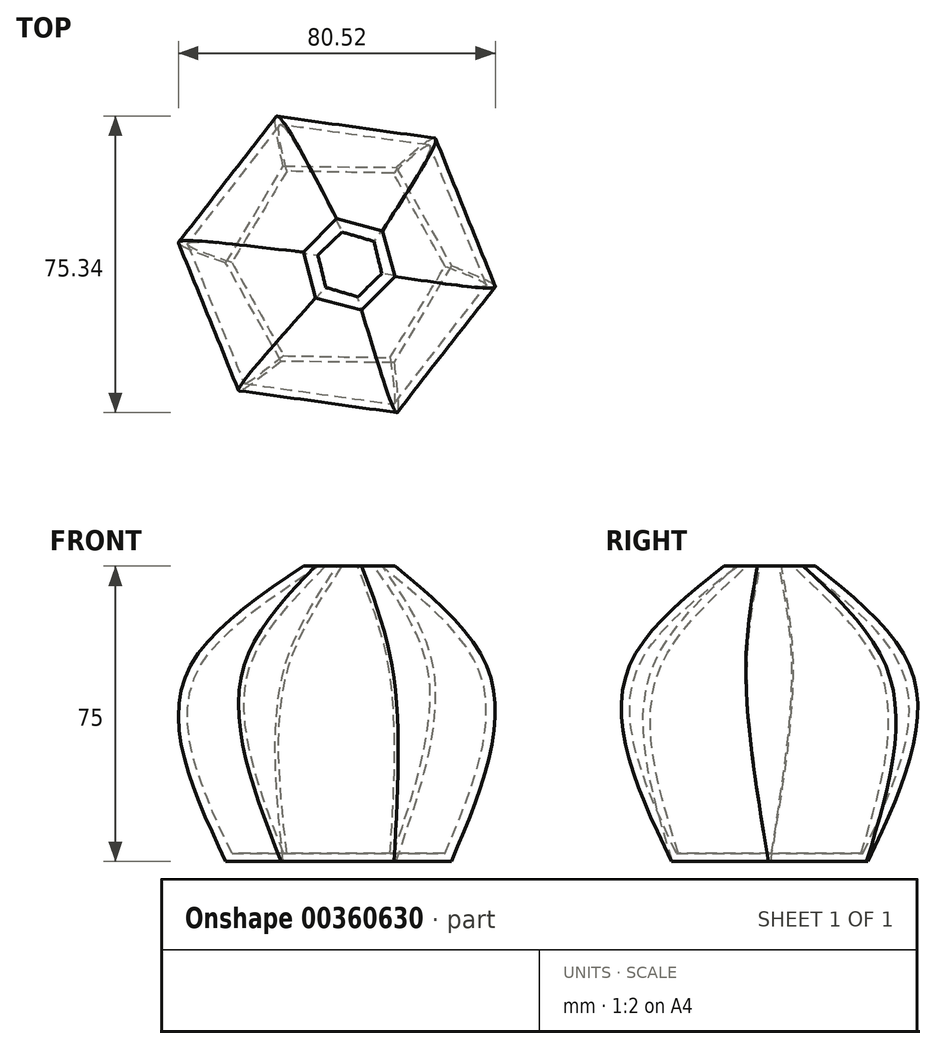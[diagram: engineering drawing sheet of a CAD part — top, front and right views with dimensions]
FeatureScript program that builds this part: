
annotation { "Feature Type Name" : "Feature", "Feature Type Description" : "" }
export const myFeature = defineFeature(function(context is Context, id is Id, definition is map)
    precondition{}
    {
        {
            var Q0;
            Q0=qCreatedBy(makeId("Top.planeOp"),FACE);
            var sketch = newSketch(context, id + "F0", { "sketchPlane" : qUnion([Q0])});
            skCircle(sketch, "E0.cCircle", {"center": v(0, 0) * mm, "radius": 24.81 * mm, "construction": true});
            skLineSegment(sketch, "E0.0", {"start": v(-28.65, 0.3) * mm, "end": v(-14.06, 24.96) * mm});
            skLineSegment(sketch, "E0.1", {"start": v(-14.06, 24.96) * mm, "end": v(14.59, 24.66) * mm});
            skLineSegment(sketch, "E0.2", {"start": v(14.59, 24.66) * mm, "end": v(28.65, -0.3) * mm});
            skLineSegment(sketch, "E0.3", {"start": v(28.65, -0.3) * mm, "end": v(14.06, -24.96) * mm});
            skLineSegment(sketch, "E0.4", {"start": v(14.06, -24.96) * mm, "end": v(-14.59, -24.66) * mm});
            skLineSegment(sketch, "E0.5", {"start": v(-14.59, -24.66) * mm, "end": v(-28.65, 0.3) * mm});
            skPoint(sketch, "E0.0.midPoint", {"position": v(-21.36, 12.63) * mm});
            skSolve(sketch);
        }
        {
            var Q0;
            Q0=qCreatedBy(makeId("Top.planeOp"),FACE);
            cPlane(context, id + "F1", {"entities" : qUnion([Q0]), "cplaneType" : CPlaneType.OFFSET, "offset" : 50 * mm, "width" : 150 * mm, "height" : 150 * mm});
        }
        {
            var Q0;
            Q0=qCreatedBy(makeId("Top.planeOp"),FACE);
            cPlane(context, id + "F2", {"entities" : qUnion([Q0]), "cplaneType" : CPlaneType.OFFSET, "offset" : 75 * mm, "width" : 150 * mm, "height" : 150 * mm});
        }
        {
            var Q0;
            Q0=qCreatedBy(id+"F1.planeOp",FACE);
            var sketch = newSketch(context, id + "F3", { "sketchPlane" : qUnion([Q0])});
            skCircle(sketch, "E1.cCircle", {"center": v(0, 0) * mm, "radius": 32.87 * mm, "construction": true});
            skLineSegment(sketch, "E1.0", {"start": v(-37.47, 6.03) * mm, "end": v(-13.51, 35.47) * mm});
            skLineSegment(sketch, "E1.1", {"start": v(-13.51, 35.47) * mm, "end": v(23.96, 29.44) * mm});
            skLineSegment(sketch, "E1.2", {"start": v(23.96, 29.44) * mm, "end": v(37.47, -6.03) * mm});
            skLineSegment(sketch, "E1.3", {"start": v(37.47, -6.03) * mm, "end": v(13.51, -35.47) * mm});
            skLineSegment(sketch, "E1.4", {"start": v(13.51, -35.47) * mm, "end": v(-23.96, -29.44) * mm});
            skLineSegment(sketch, "E1.5", {"start": v(-23.96, -29.44) * mm, "end": v(-37.47, 6.03) * mm});
            skPoint(sketch, "E1.0.midPoint", {"position": v(-25.5, 20.75) * mm});
            skSolve(sketch);
        }
        {
            var Q0;
            Q0=qCreatedBy(id+"F2.planeOp",FACE);
            var sketch = newSketch(context, id + "F4", { "sketchPlane" : qUnion([Q0])});
            skCircle(sketch, "E2.cCircle", {"center": v(2.66, 0) * mm, "radius": 10.41 * mm, "construction": true});
            skLineSegment(sketch, "E2.0", {"start": v(5.81, -11.6) * mm, "end": v(-5.81, -8.53) * mm});
            skLineSegment(sketch, "E2.1", {"start": v(-5.81, -8.53) * mm, "end": v(-8.96, 3.08) * mm});
            skLineSegment(sketch, "E2.2", {"start": v(-8.96, 3.08) * mm, "end": v(-0.48, 11.6) * mm});
            skLineSegment(sketch, "E2.3", {"start": v(-0.48, 11.6) * mm, "end": v(11.14, 8.53) * mm});
            skLineSegment(sketch, "E2.4", {"start": v(11.14, 8.53) * mm, "end": v(14.29, -3.08) * mm});
            skLineSegment(sketch, "E2.5", {"start": v(14.29, -3.08) * mm, "end": v(5.81, -11.6) * mm});
            skPoint(sketch, "E2.0.midPoint", {"position": v(0, -10.07) * mm});
            skSolve(sketch);
        }
        {
            var Q0;
            Q0=makeQuery(id+"F0.imprint","IMPRINT",FACE,{"disambiguationData":[TD([[makeQuery(id+"F0.imprint","IMPRINT",EDGE,{"derivedFrom":sQuery(id+"F0.wireOp",EDGE,"E0.0")}),-1.0]])]});
            var Q1;
            Q1=makeQuery(id+"F3.imprint","IMPRINT",FACE,{"disambiguationData":[TD([[makeQuery(id+"F3.imprint","IMPRINT",EDGE,{"derivedFrom":sQuery(id+"F3.wireOp",EDGE,"E1.0")}),-1.0]])]});
            var Q2;
            Q2=makeQuery(id+"F4.imprint","IMPRINT",FACE,{"disambiguationData":[TD([[makeQuery(id+"F4.imprint","IMPRINT",EDGE,{"derivedFrom":sQuery(id+"F4.wireOp",EDGE,"E2.0")}),-1.0]])]});
            loft(context, id + "F5", {"sheetProfilesArray" : [{ "sheetProfileEntities" : qUnion([Q0]) }, { "sheetProfileEntities" : qUnion([Q1]) }, { "sheetProfileEntities" : qUnion([Q2]) }]});
        }
        {
            var Q0;
            Q0=makeQuery(id+"F5.opLoft","CAP_FACE",FACE,{"disambiguationData":[OSD([makeQuery(id+"F4.imprint","IMPRINT",FACE,{"disambiguationData":[TD([[makeQuery(id+"F4.imprint","IMPRINT",EDGE,{"derivedFrom":sQuery(id+"F4.wireOp",EDGE,"E2.0")}),-1.0]])]})])],"isStart":true});
            shell(context, id + "F6", {"entities" : qUnion([Q0]), "thickness" : 2 * mm});
        }
    });
